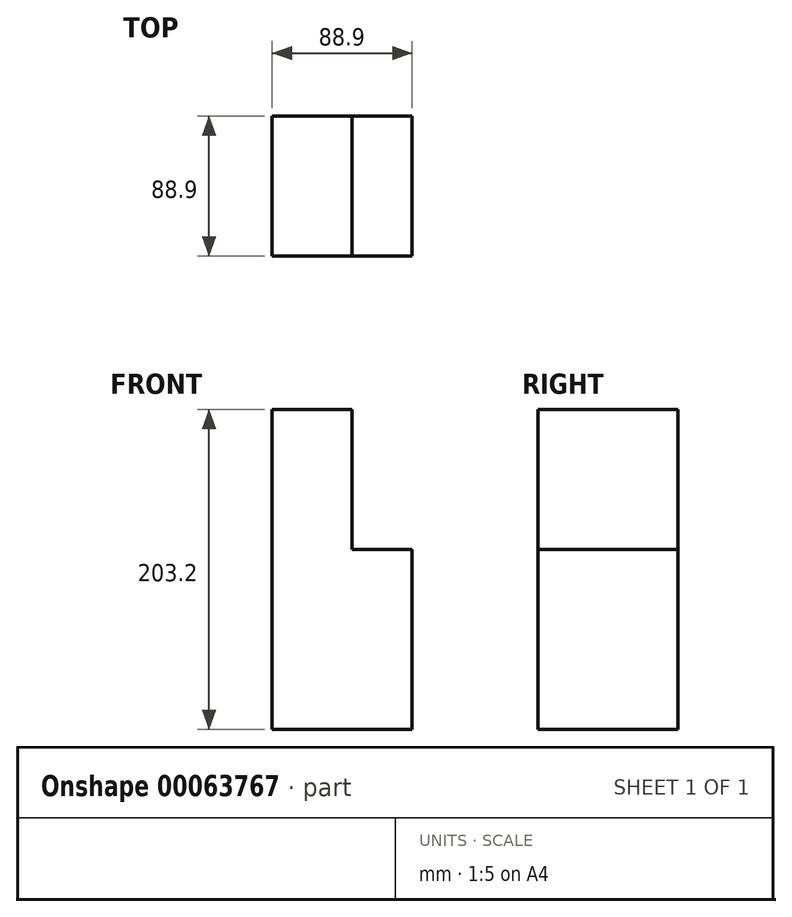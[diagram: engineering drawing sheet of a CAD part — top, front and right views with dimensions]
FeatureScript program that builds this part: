
annotation { "Feature Type Name" : "Feature", "Feature Type Description" : "" }
export const myFeature = defineFeature(function(context is Context, id is Id, definition is map)
    precondition{}
    {
        {
            var Q0;
            Q0=qCreatedBy(makeId("Top.planeOp"),FACE);
            var sketch = newSketch(context, id + "F0", { "sketchPlane" : qUnion([Q0])});
            skLineSegment(sketch, "E0.bottom", {"start": v(-41.76, 43.96) * mm, "end": v(47.14, 43.96) * mm});
            skLineSegment(sketch, "E0.top", {"start": v(-41.76, -44.94) * mm, "end": v(47.14, -44.94) * mm});
            skLineSegment(sketch, "E0.left", {"start": v(-41.76, 43.96) * mm, "end": v(-41.76, -44.94) * mm});
            skLineSegment(sketch, "E0.right", {"start": v(47.14, 43.96) * mm, "end": v(47.14, -44.94) * mm});
            skSolve(sketch);
        }
        {
            var Q0;
            Q0=qSketchRegion(id+"F0",true);
            extrude(context, id + "F1", {"entities" : qUnion([Q0]), "depth" : 203.2 * mm});
        }
        {
            var Q0;
            Q0=makeQuery(id+"F1.opExtrude","CAP_FACE",FACE,{"disambiguationData":[OSD([sQuery(id+"F0.wireOp",EDGE,"E0.bottom"),sQuery(id+"F0.wireOp",EDGE,"E0.top"),sQuery(id+"F0.wireOp",EDGE,"E0.left"),sQuery(id+"F0.wireOp",EDGE,"E0.right")])],"isStart":false});
            var sketch = newSketch(context, id + "F2", { "sketchPlane" : qUnion([Q0])});
            skLineSegment(sketch, "E1.0", {"start": v(9.04, 43.96) * mm, "end": v(47.14, 43.96) * mm});
            skLineSegment(sketch, "E2.0", {"start": v(47.14, 43.96) * mm, "end": v(47.14, -44.94) * mm});
            skLineSegment(sketch, "E3.right", {"start": v(47.14, 43.96) * mm, "end": v(47.14, 5.86) * mm});
            skLineSegment(sketch, "E4.bottom", {"start": v(47.14, 43.96) * mm, "end": v(9.04, 43.96) * mm});
            skLineSegment(sketch, "E4.top", {"start": v(47.14, -44.94) * mm, "end": v(9.04, -44.94) * mm});
            skLineSegment(sketch, "E4.right", {"start": v(9.04, 5.86) * mm, "end": v(9.04, -44.94) * mm});
            skLineSegment(sketch, "E5", {"start": v(9.04, 5.86) * mm, "end": v(9.04, 43.96) * mm});
            skPoint(sketch, "E6.orphan", {"position": v(-41.76, 43.96) * mm});
            skSolve(sketch);
        }
        {
            var Q0;
            Q0=qSketchRegion(id+"F2",true);
            extrude(context, id + "F3", {"entities" : qUnion([Q0]), "operationType" : NewBodyOperationType.REMOVE, "oppositeDirection" : true, "depth" : 88.9 * mm});
        }
    });
